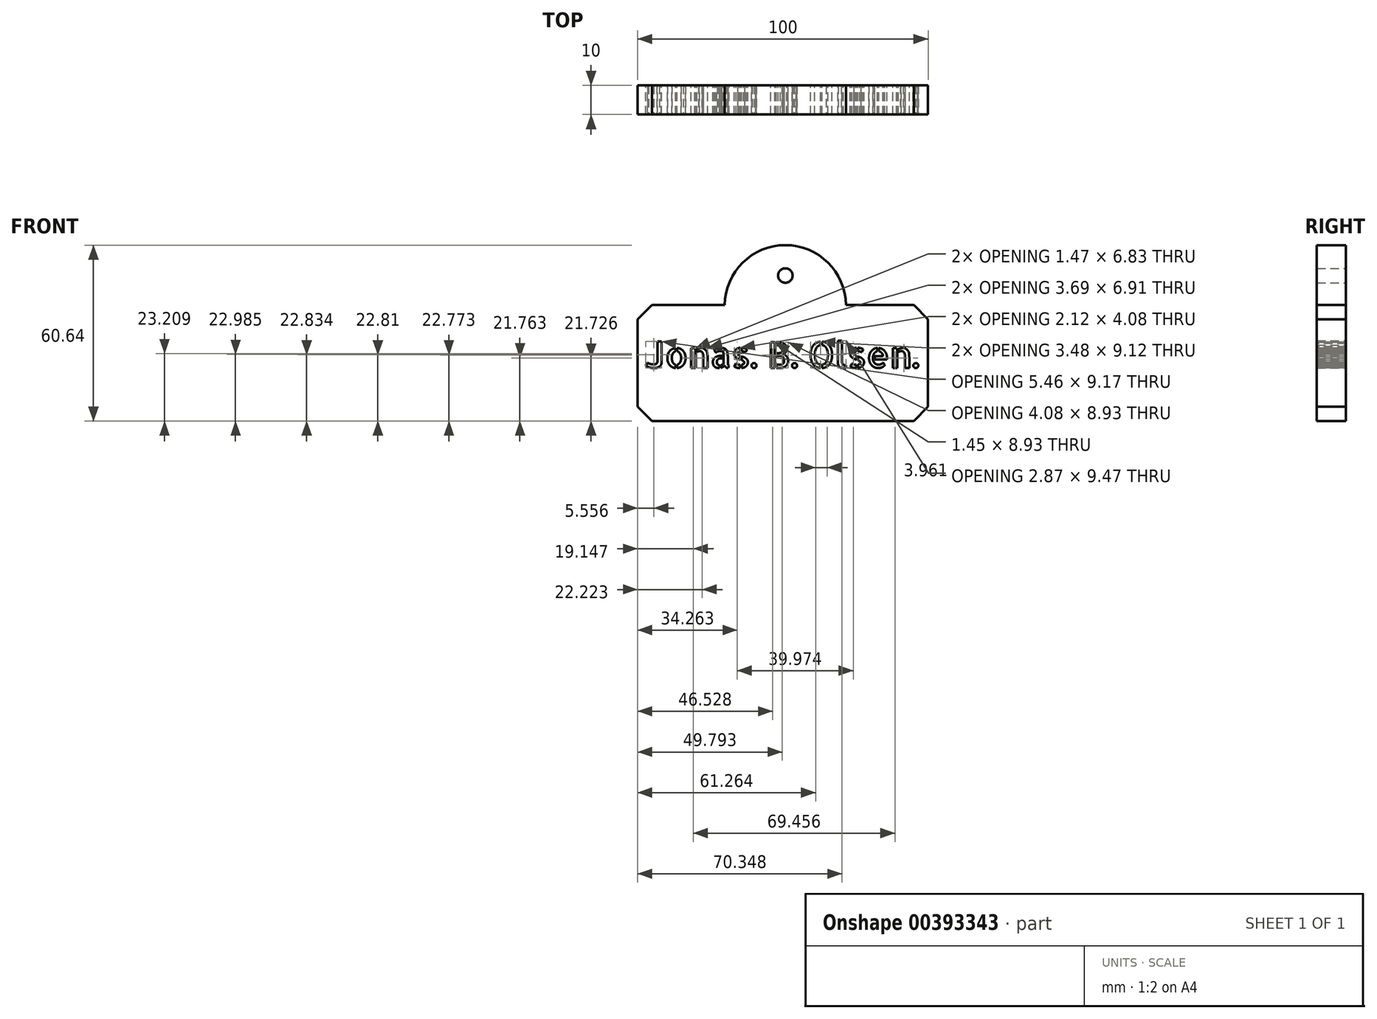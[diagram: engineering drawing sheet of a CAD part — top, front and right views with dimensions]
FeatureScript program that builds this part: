
annotation { "Feature Type Name" : "Feature", "Feature Type Description" : "" }
export const myFeature = defineFeature(function(context is Context, id is Id, definition is map)
    precondition{}
    {
        {
            var Q0;
            Q0=qCreatedBy(makeId("Front.planeOp"),FACE);
            var sketch = newSketch(context, id + "F0", { "sketchPlane" : qUnion([Q0])});
            skLineSegment(sketch, "E0.top", {"start": v(-50.86, 1.09) * mm, "end": v(49.14, 1.09) * mm});
            skLineSegment(sketch, "E0.left", {"start": v(-50.86, 41.09) * mm, "end": v(-50.86, 1.09) * mm});
            skLineSegment(sketch, "E0.right", {"start": v(49.14, 41.09) * mm, "end": v(49.14, 1.09) * mm});
            skPoint(sketch, "E1", {"position": v(0, 40.87) * mm});
            skArc(sketch, "E2", {"start": v(20.86, 41.09) * mm, "mid": v(0, 61.73) * mm, "end": v(-20.86, 41.09) * mm});
            skLineSegment(sketch, "E3", {"start": v(-50.86, 41.09) * mm, "end": v(-20.86, 41.09) * mm});
            skLineSegment(sketch, "E4", {"start": v(49.14, 41.09) * mm, "end": v(20.86, 41.09) * mm});
            skCircle(sketch, "E5", {"center": v(0, 51.23) * mm, "radius": 2.5 * mm});
            skText(sketch, "E6", { "text": "Jonas. B. Olsen.", "fontName": "AllertaStencil-Regular.ttf"});
            const initialGuessF0  = {"E6": [-0.04835, 0.0194, 1, 0, 0.00893]};
            skSetInitialGuess(sketch, initialGuessF0);
            skSolve(sketch);
        }
        {
            var Q0;
            Q0 = qSketchRegion(id + "F0", true);
            extrude(context, id + "F1", {"entities" : qUnion([Q0]), "depth" : 10 * mm});
        }
        {
            var Q0;
            Q0=makeQuery(id+"F1.opExtrude","SWEPT_EDGE",EDGE,{"disambiguationData":[OSD([sQuery(id+"F0.wireOp",EDGE,"E0.left"),sQuery(id+"F0.wireOp",EDGE,"E3")])]});
            var Q1;
            Q1=makeQuery(id+"F1.opExtrude","SWEPT_EDGE",EDGE,{"disambiguationData":[OSD([sQuery(id+"F0.wireOp",EDGE,"E0.top"),sQuery(id+"F0.wireOp",EDGE,"E0.left")])]});
            var Q2;
            Q2=makeQuery(id+"F1.opExtrude","SWEPT_EDGE",EDGE,{"disambiguationData":[OSD([sQuery(id+"F0.wireOp",EDGE,"E0.right"),sQuery(id+"F0.wireOp",EDGE,"E4")])]});
            var Q3;
            Q3=makeQuery(id+"F1.opExtrude","SWEPT_EDGE",EDGE,{"disambiguationData":[OSD([sQuery(id+"F0.wireOp",EDGE,"E0.top"),sQuery(id+"F0.wireOp",EDGE,"E0.right")])]});
            chamfer(context, id + "F2", {"entities" : qUnion([Q0, Q1, Q2, Q3]), "width" : 4.9 * mm, "tangentPropagation" : true});
        }
    });
